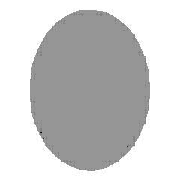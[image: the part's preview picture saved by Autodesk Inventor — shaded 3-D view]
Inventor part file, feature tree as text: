
AUTODESK INVENTOR PART (.ipt)
format: ipt  version: 2013 (Build 170138000, 138)  size: 110,080 bytes
history: native  units: mm (DEFAULTED — no unit token found)
features: other x4, sketch x3, plane x2, split x1
ambient origin geometry x8: Origin, YZ Plane, XZ Plane, XY Plane, X Axis, Y Axis, Z Axis, Center Point
bodies: Solid1 (feature_tree), Body (feature_tree)
feature tree (10):
  parser-record x1  (decoder bookkeeping rows leaked as tree rows — omitted from the tree; the rows remain in map.json)
  other  "Driven Length"
  other  "Start plane"
  other  "End plane"
  plane  "Work Plane4"
  split  "Split1"
  sketch  "Sketch"  dims[d2=0.0mm d4=-19.05mm d5=304.8mm d6=90.0deg d7=323.85mm]
  sketch  "Sketch2"  dims[d0=38.1mm]
  plane  "Work Plane3"
  sketch  "Sketch3"  dims[d1=323.85mm]
